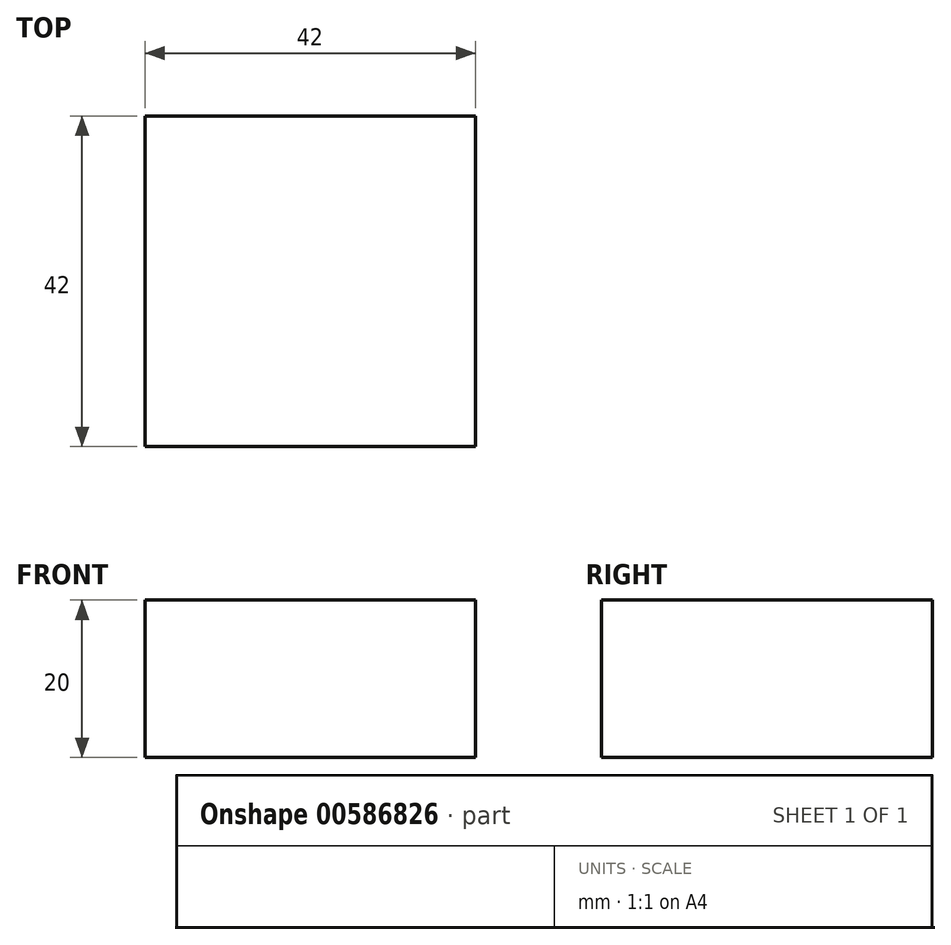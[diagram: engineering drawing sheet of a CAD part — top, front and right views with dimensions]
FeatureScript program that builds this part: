
annotation { "Feature Type Name" : "Feature", "Feature Type Description" : "" }
export const myFeature = defineFeature(function(context is Context, id is Id, definition is map)
    precondition{}
    {
        {
            var Q0;
            Q0=qCreatedBy(makeId("Top.planeOp"),FACE);
            var sketch = newSketch(context, id + "F0", { "sketchPlane" : qUnion([Q0])});
            skLineSegment(sketch, "E0.bottom", {"start": v(-62.32, 53.07) * mm, "end": v(-20.32, 53.07) * mm});
            skLineSegment(sketch, "E0.top", {"start": v(-62.32, 11.07) * mm, "end": v(-20.32, 11.07) * mm});
            skLineSegment(sketch, "E0.left", {"start": v(-62.32, 53.07) * mm, "end": v(-62.32, 11.07) * mm});
            skLineSegment(sketch, "E0.right", {"start": v(-20.32, 53.07) * mm, "end": v(-20.32, 11.07) * mm});
            skSolve(sketch);
        }
        {
            var Q0;
            Q0=makeQuery(id+"F0.imprint","IMPRINT",FACE,{"disambiguationData":[TD([[makeQuery(id+"F0.imprint","IMPRINT",EDGE,{"derivedFrom":sQuery(id+"F0.wireOp",EDGE,"E0.bottom")}),-1.0]])]});
            extrude(context, id + "F1", {"entities" : qUnion([Q0]), "depth" : 20 * mm, "offsetDistance" : 25 * mm});
        }
    });
